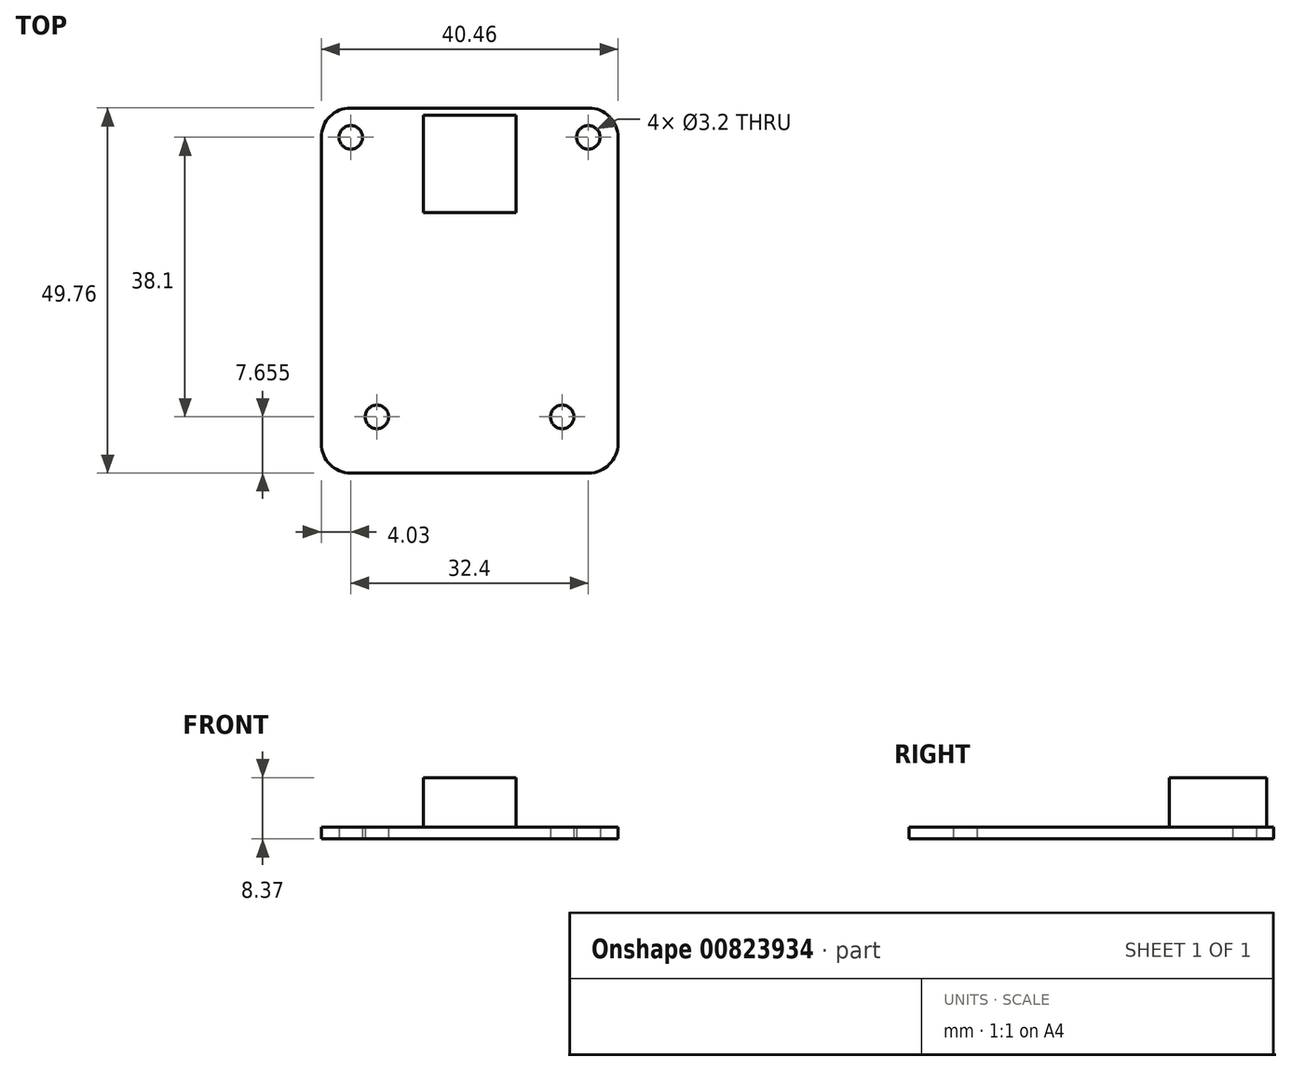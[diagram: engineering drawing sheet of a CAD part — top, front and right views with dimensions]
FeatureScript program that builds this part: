
annotation { "Feature Type Name" : "Feature", "Feature Type Description" : "" }
export const myFeature = defineFeature(function(context is Context, id is Id, definition is map)
    precondition{}
    {
        {
            var Q0;
            Q0=qCreatedBy(makeId("Top.planeOp"),FACE);
            var sketch = newSketch(context, id + "F0", { "sketchPlane" : qUnion([Q0])});
            skLineSegment(sketch, "E0.bottom", {"start": v(16.23, -24.87) * mm, "end": v(-16.23, -24.88) * mm});
            skLineSegment(sketch, "E0.top", {"start": v(16.23, 24.88) * mm, "end": v(-16.23, 24.87) * mm});
            skLineSegment(sketch, "E0.left", {"start": v(20.23, -20.87) * mm, "end": v(20.23, 20.88) * mm});
            skLineSegment(sketch, "E0.right", {"start": v(-20.23, -20.88) * mm, "end": v(-20.23, 20.87) * mm});
            skPoint(sketch, "E0.middle", {"position": v(0, 0) * mm});
            skPoint(sketch, "E1.visualSharp", {"position": v(-20.23, 24.87) * mm});
            skArc(sketch, "E1.filletArc", {"start": v(-16.23, 24.87) * mm, "mid": v(-19.06, 23.7) * mm, "end": v(-20.23, 20.87) * mm});
            skPoint(sketch, "E2.visualSharp", {"position": v(20.23, 24.88) * mm});
            skArc(sketch, "E2.filletArc", {"start": v(20.23, 20.88) * mm, "mid": v(19.06, 23.7) * mm, "end": v(16.23, 24.88) * mm});
            skPoint(sketch, "E3.visualSharp", {"position": v(20.23, -24.87) * mm});
            skArc(sketch, "E3.filletArc", {"start": v(16.23, -24.87) * mm, "mid": v(19.06, -23.7) * mm, "end": v(20.23, -20.87) * mm});
            skPoint(sketch, "E4.visualSharp", {"position": v(-20.23, -24.88) * mm});
            skArc(sketch, "E4.filletArc", {"start": v(-20.23, -20.88) * mm, "mid": v(-19.06, -23.7) * mm, "end": v(-16.23, -24.88) * mm});
            skCircle(sketch, "E5", {"center": v(-16.2, 20.87) * mm, "radius": 1.6 * mm});
            skLineSegment(sketch, "E6", {"start": v(0, 0) * mm, "end": v(0, 34.48) * mm, "construction": true});
            skCircle(sketch, "E7.MirrorC", {"center": v(16.2, 20.87) * mm, "radius": 1.6 * mm});
            skCircle(sketch, "E8", {"center": v(-12.63, -17.23) * mm, "radius": 1.6 * mm});
            skCircle(sketch, "E9.MirrorC", {"center": v(12.63, -17.23) * mm, "radius": 1.6 * mm});
            skSolve(sketch);
        }
        {
            var Q0;
            Q0=makeQuery(id+"F0.imprint","IMPRINT",FACE,{"disambiguationData":[TD([[makeQuery(id+"F0.imprint","IMPRINT",EDGE,{"derivedFrom":sQuery(id+"F0.wireOp",EDGE,"E0.bottom")}),-1.0]])]});
            extrude(context, id + "F1", {"entities" : qUnion([Q0]), "depth" : 1.6 * mm, "offsetDistance" : 25 * mm});
        }
        {
            var Q0;
            Q0=makeQuery(id+"F1.opExtrude","CAP_FACE",FACE,{"disambiguationData":[OSD([sQuery(id+"F0.wireOp",EDGE,"E0.bottom"),sQuery(id+"F0.wireOp",EDGE,"E0.top"),sQuery(id+"F0.wireOp",EDGE,"E0.left"),sQuery(id+"F0.wireOp",EDGE,"E0.right"),sQuery(id+"F0.wireOp",EDGE,"E1.filletArc"),sQuery(id+"F0.wireOp",EDGE,"E2.filletArc"),sQuery(id+"F0.wireOp",EDGE,"E3.filletArc"),sQuery(id+"F0.wireOp",EDGE,"E4.filletArc"),sQuery(id+"F0.wireOp",EDGE,"E5"),sQuery(id+"F0.wireOp",EDGE,"E7.MirrorC"),sQuery(id+"F0.wireOp",EDGE,"E8"),sQuery(id+"F0.wireOp",EDGE,"E9.MirrorC")])],"isStart":false});
            var sketch = newSketch(context, id + "F2", { "sketchPlane" : qUnion([Q0])});
            skLineSegment(sketch, "E10.bottom", {"start": v(6.32, 10.62) * mm, "end": v(-6.32, 10.62) * mm});
            skLineSegment(sketch, "E10.top", {"start": v(6.32, 23.88) * mm, "end": v(-6.32, 23.88) * mm});
            skLineSegment(sketch, "E10.left", {"start": v(6.32, 10.62) * mm, "end": v(6.32, 23.88) * mm});
            skLineSegment(sketch, "E10.right", {"start": v(-6.32, 10.62) * mm, "end": v(-6.32, 23.88) * mm});
            skPoint(sketch, "E10.middle", {"position": v(0, 17.25) * mm});
            skSolve(sketch);
        }
        {
            var Q0;
            Q0=makeQuery(id+"F2.imprint","IMPRINT",FACE,{"disambiguationData":[TD([[makeQuery(id+"F2.imprint","IMPRINT",EDGE,{"derivedFrom":sQuery(id+"F2.wireOp",EDGE,"E10.bottom")}),-1.0]])]});
            extrude(context, id + "F3", {"entities" : qUnion([Q0]), "operationType" : NewBodyOperationType.ADD, "depth" : 6.77 * mm, "offsetDistance" : 25 * mm});
        }
    });
